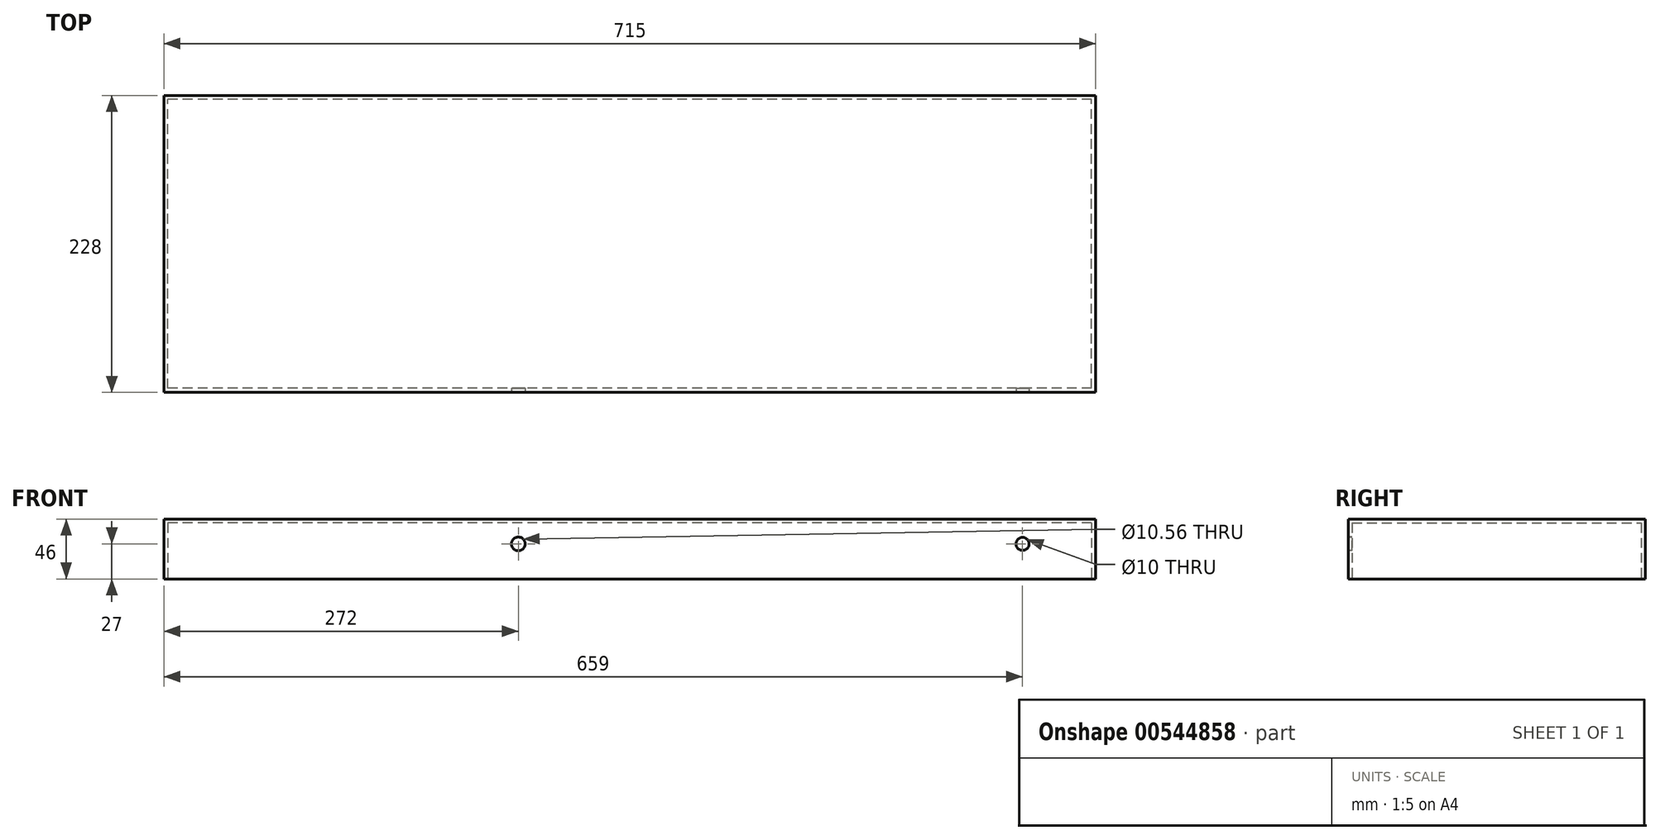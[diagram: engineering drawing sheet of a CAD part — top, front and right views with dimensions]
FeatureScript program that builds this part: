
annotation { "Feature Type Name" : "Feature", "Feature Type Description" : "" }
export const myFeature = defineFeature(function(context is Context, id is Id, definition is map)
    precondition{}
    {
        {
            var Q0;
            Q0=qCreatedBy(makeId("Right.planeOp"),FACE);
            var sketch = newSketch(context, id + "F0", { "sketchPlane" : qUnion([Q0])});
            skLineSegment(sketch, "E0.bottom", {"start": v(-48.81, 19.57) * mm, "end": v(179.19, 19.57) * mm});
            skLineSegment(sketch, "E0.top", {"start": v(-48.81, -26.43) * mm, "end": v(179.19, -26.43) * mm});
            skLineSegment(sketch, "E0.left", {"start": v(-48.81, 19.57) * mm, "end": v(-48.81, -26.43) * mm});
            skLineSegment(sketch, "E0.right", {"start": v(179.19, 19.57) * mm, "end": v(179.19, -26.43) * mm});
            skSolve(sketch);
        }
        {
            var Q0;
            Q0 = qSketchRegion(id + "F0", true);
            extrude(context, id + "F1", {"entities" : qUnion([Q0]), "depth" : 715 * mm, "offsetDistance" : 25 * mm});
        }
        {
            var Q0;
            Q0=makeQuery(id+"F1.opExtrude","SWEPT_FACE",FACE,{"disambiguationData":[OSD([sQuery(id+"F0.wireOp",EDGE,"E0.top")])]});
            shell(context, id + "F2", {"entities" : qUnion([Q0]), "thickness" : 3 * mm});
        }
        {
            var Q0;
            Q0=makeQuery(id+"F1.opExtrude","SWEPT_FACE",FACE,{"disambiguationData":[OSD([sQuery(id+"F0.wireOp",EDGE,"E0.left")])]});
            var sketch = newSketch(context, id + "F3", { "sketchPlane" : qUnion([Q0])});
            skCircle(sketch, "E1", {"center": v(659, 0.57) * mm, "radius": 5 * mm});
            skCircle(sketch, "E2", {"center": v(272, 0.57) * mm, "radius": 5.28 * mm});
            skLineSegment(sketch, "E3", {"start": v(659, 0.57) * mm, "end": v(272, 0.57) * mm, "construction": true});
            skSolve(sketch);
        }
        {
            var Q0;
            Q0 = qSketchRegion(id + "F3", true);
            extrude(context, id + "F4", {"entities" : qUnion([Q0]), "operationType" : NewBodyOperationType.REMOVE, "oppositeDirection" : true, "depth" : 3 * mm, "offsetDistance" : 25 * mm});
        }
    });
